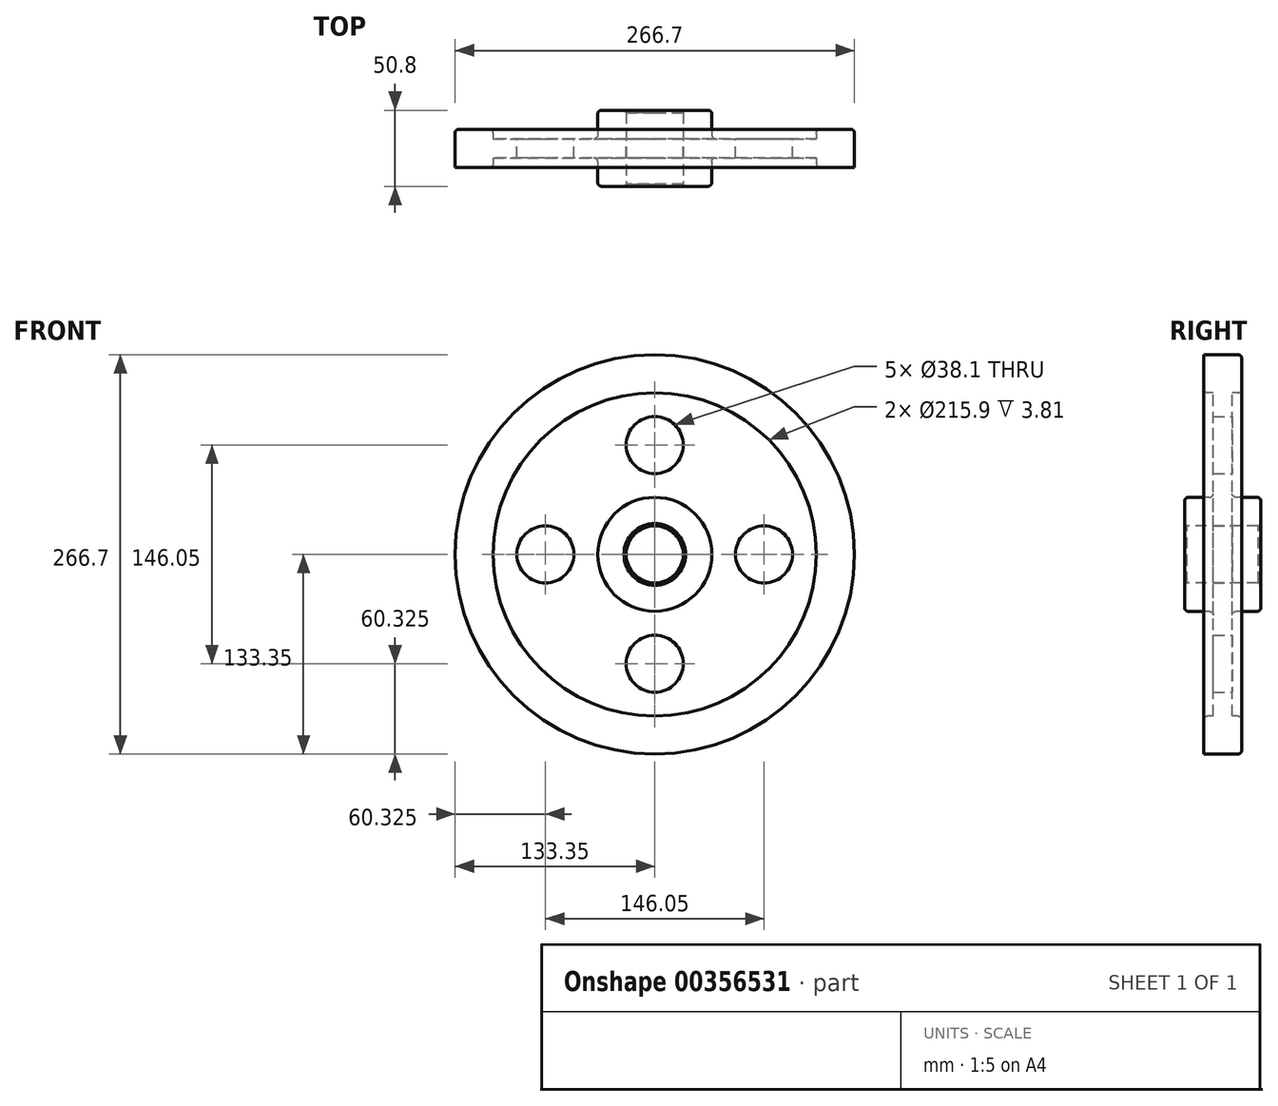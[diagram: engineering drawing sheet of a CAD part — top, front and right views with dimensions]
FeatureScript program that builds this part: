
annotation { "Feature Type Name" : "Feature", "Feature Type Description" : "" }
export const myFeature = defineFeature(function(context is Context, id is Id, definition is map)
    precondition{}
    {
        {
            var Q0;
            Q0=qCreatedBy(makeId("Right.planeOp"),FACE);
            var sketch = newSketch(context, id + "F0", { "sketchPlane" : qUnion([Q0])});
            skLineSegment(sketch, "E0", {"start": v(0, 0) * mm, "end": v(0, 28.57) * mm});
            skLineSegment(sketch, "E1", {"start": v(0, 28.57) * mm, "end": v(0, 73.03) * mm});
            skLineSegment(sketch, "E2", {"start": v(0, 73.03) * mm, "end": v(0, 120.65) * mm});
            skLineSegment(sketch, "E3.bottom", {"start": v(25.4, 19.05) * mm, "end": v(-25.4, 19.05) * mm});
            skLineSegment(sketch, "E3.top", {"start": v(25.4, 38.1) * mm, "end": v(6.35, 38.1) * mm});
            skLineSegment(sketch, "E3.left", {"start": v(25.4, 19.05) * mm, "end": v(25.4, 38.1) * mm});
            skLineSegment(sketch, "E3.right", {"start": v(-25.4, 19.05) * mm, "end": v(-25.4, 38.1) * mm});
            skPoint(sketch, "E3.middle", {"position": v(0, 28.57) * mm});
            skLineSegment(sketch, "E4.bottom", {"start": v(12.7, 107.95) * mm, "end": v(6.35, 107.95) * mm});
            skLineSegment(sketch, "E4.top", {"start": v(12.7, 133.35) * mm, "end": v(-12.7, 133.35) * mm});
            skLineSegment(sketch, "E4.left", {"start": v(12.7, 107.95) * mm, "end": v(12.7, 133.35) * mm});
            skLineSegment(sketch, "E4.right", {"start": v(-12.7, 107.95) * mm, "end": v(-12.7, 133.35) * mm});
            skPoint(sketch, "E4.middle", {"position": v(0, 120.65) * mm});
            skLineSegment(sketch, "E5.left", {"start": v(6.35, 28.58) * mm, "end": v(6.35, 117.48) * mm});
            skLineSegment(sketch, "E5.right", {"start": v(-6.35, 28.58) * mm, "end": v(-6.35, 117.48) * mm});
            skPoint(sketch, "E5.middle", {"position": v(0, 73.03) * mm});
            skLineSegment(sketch, "E6.trimOffspring", {"start": v(-6.35, 107.95) * mm, "end": v(-12.7, 107.95) * mm});
            skLineSegment(sketch, "E7.trimOffspring", {"start": v(-6.35, 38.1) * mm, "end": v(-25.4, 38.1) * mm});
            skLineSegment(sketch, "E8", {"start": v(0, 0) * mm, "end": v(25.32, 0) * mm});
            skSolve(sketch);
        }
        {
            var Q0;
            {var subQ4=sQuery(id+"F0.wireOp",EDGE,"E3.top");Q0=makeQuery(id+"F0.imprint","IMPRINT",FACE,{"disambiguationData":[TD([[makeQuery(id+"F0.imprint","IMPRINT",EDGE,{"derivedFrom":subQ4}),1.0]])]});}
            var Q1;
            Q1=sQuery(id+"F0.wireOp",EDGE,"E8");
            revolve(context, id + "F1", {"entities" : qUnion([Q0]), "axis" : qUnion([Q1]), "revolveType" : RevolveType.FULL});
        }
        {
            var Q0;
            Q0=makeQuery(id+"F1.opRevolve","SWEPT_FACE",FACE,{"disambiguationData":[OSD([sQuery(id+"F0.wireOp",EDGE,"E5.left")])]});
            var sketch = newSketch(context, id + "F2", { "sketchPlane" : qUnion([Q0])});
            skLineSegment(sketch, "E9", {"start": v(0, 0) * mm, "end": v(0, 73.03) * mm});
            skCircle(sketch, "E10", {"center": v(0, 73.03) * mm, "radius": 19.05 * mm});
            skCircle(sketch, "E11.1.0", {"center": v(-73.03, 0) * mm, "radius": 19.05 * mm});
            skCircle(sketch, "E11.2.0", {"center": v(0, -73.03) * mm, "radius": 19.05 * mm});
            skCircle(sketch, "E11.3.0", {"center": v(73.03, 0) * mm, "radius": 19.05 * mm});
            skPoint(sketch, "E11.center", {"position": v(0, 0) * mm});
            skSolve(sketch);
        }
        {
            var Q0;
            Q0=makeQuery(id+"F2.imprint","IMPRINT",FACE,{"disambiguationData":[TD([[makeQuery(id+"F2.imprint","IMPRINT",EDGE,{"derivedFrom":sQuery(id+"F2.wireOp",EDGE,"E11.1.0")}),1.0]])]});
            var Q1;
            Q1=makeQuery(id+"F2.imprint","IMPRINT",FACE,{"disambiguationData":[TD([[makeQuery(id+"F2.imprint","IMPRINT",EDGE,{"derivedFrom":sQuery(id+"F2.wireOp",EDGE,"E11.2.0")}),1.0]])]});
            var Q2;
            Q2=makeQuery(id+"F2.imprint","IMPRINT",FACE,{"disambiguationData":[TD([[makeQuery(id+"F2.imprint","IMPRINT",EDGE,{"derivedFrom":sQuery(id+"F2.wireOp",EDGE,"E11.3.0")}),1.0]])]});
            var Q3;
            Q3=makeQuery(id+"F2.imprint","IMPRINT",FACE,{"disambiguationData":[TD([[makeQuery(id+"F2.imprint","IMPRINT",EDGE,{"derivedFrom":sQuery(id+"F2.wireOp",EDGE,"E10")}),1.0]])]});
            extrude(context, id + "F3", {"entities" : qUnion([Q0, Q1, Q2, Q3]), "operationType" : NewBodyOperationType.REMOVE, "oppositeDirection" : true, "depth" : 25.4 * mm});
        }
        {
            var Q0;
            Q0=makeQuery(id+"F1.opRevolve","SWEPT_EDGE",EDGE,{"disambiguationData":[OSD([sQuery(id+"F0.wireOp",EDGE,"E3.top"),sQuery(id+"F0.wireOp",EDGE,"E3.left")])]});
            var Q1;
            Q1=makeQuery(id+"F1.opRevolve","SWEPT_EDGE",EDGE,{"disambiguationData":[OSD([sQuery(id+"F0.wireOp",EDGE,"E3.top"),sQuery(id+"F0.wireOp",EDGE,"E5.left")])]});
            var Q2;
            Q2=makeQuery(id+"F1.opRevolve","SWEPT_EDGE",EDGE,{"disambiguationData":[OSD([sQuery(id+"F0.wireOp",EDGE,"E4.bottom"),sQuery(id+"F0.wireOp",EDGE,"E4.left")])]});
            var Q3;
            Q3=makeQuery(id+"F1.opRevolve","SWEPT_EDGE",EDGE,{"disambiguationData":[OSD([sQuery(id+"F0.wireOp",EDGE,"E4.top"),sQuery(id+"F0.wireOp",EDGE,"E4.left")])]});
            var Q4;
            Q4=makeQuery(id+"F1.opRevolve","SWEPT_EDGE",EDGE,{"disambiguationData":[OSD([sQuery(id+"F0.wireOp",EDGE,"E4.right"),sQuery(id+"F0.wireOp",EDGE,"E6.trimOffspring")])]});
            var Q5;
            Q5=makeQuery(id+"F1.opRevolve","SWEPT_EDGE",EDGE,{"disambiguationData":[OSD([sQuery(id+"F0.wireOp",EDGE,"E3.right"),sQuery(id+"F0.wireOp",EDGE,"E7.trimOffspring")])]});
            var Q6;
            Q6=makeQuery(id+"F1.opRevolve","SWEPT_EDGE",EDGE,{"disambiguationData":[OSD([sQuery(id+"F0.wireOp",EDGE,"E5.right"),sQuery(id+"F0.wireOp",EDGE,"E7.trimOffspring")])]});
            fillet(context, id + "F4", {"entities" : qUnion([Q0, Q1, Q2, Q3, Q4, Q5, Q6]), "radius" : 2.54 * mm, "tangentPropagation" : true, "allowEdgeOverflow" : false});
        }
        {
            var Q0;
            Q0=makeQuery(id+"F1.opRevolve","SWEPT_EDGE",EDGE,{"disambiguationData":[OSD([sQuery(id+"F0.wireOp",EDGE,"E3.bottom"),sQuery(id+"F0.wireOp",EDGE,"E3.left")])]});
            var Q1;
            Q1=makeQuery(id+"F1.opRevolve","SWEPT_EDGE",EDGE,{"disambiguationData":[OSD([sQuery(id+"F0.wireOp",EDGE,"E3.bottom"),sQuery(id+"F0.wireOp",EDGE,"E3.right")])]});
            chamfer(context, id + "F5", {"entities" : qUnion([Q0, Q1]), "width" : 1.59 * mm, "tangentPropagation" : true});
        }
    });
